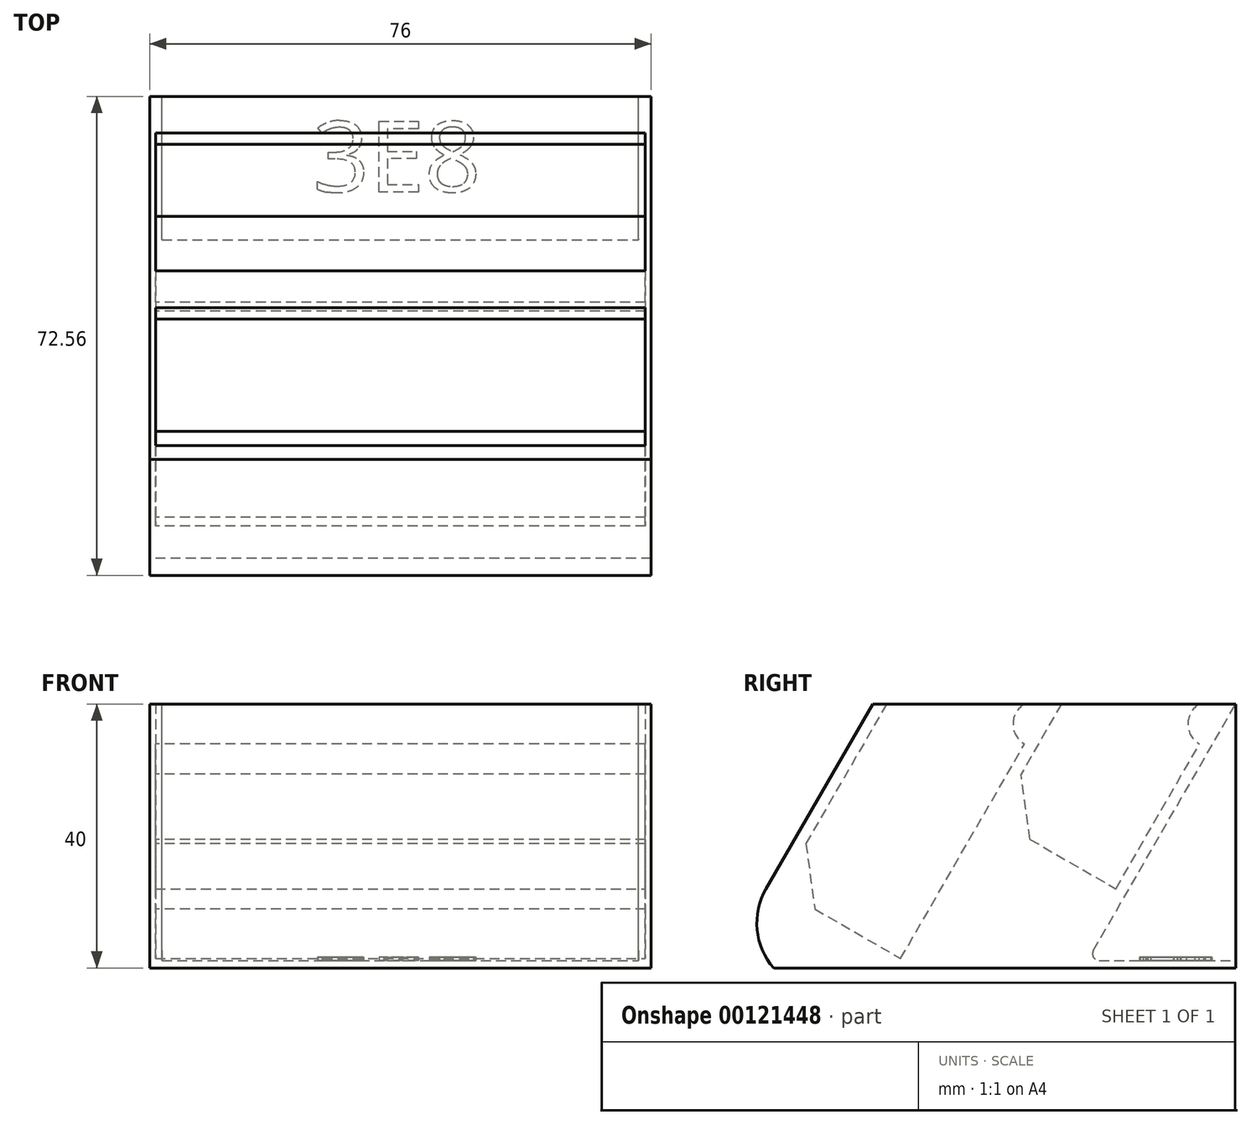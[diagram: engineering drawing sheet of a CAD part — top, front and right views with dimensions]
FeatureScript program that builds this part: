
annotation { "Feature Type Name" : "Feature", "Feature Type Description" : "" }
export const myFeature = defineFeature(function(context is Context, id is Id, definition is map)
    precondition{}
    {
        {
            var Q0;
            Q0=qCreatedBy(makeId("Right.planeOp"),FACE);
            var sketch = newSketch(context, id + "F0", { "sketchPlane" : qUnion([Q0])});
            skLineSegment(sketch, "E0", {"start": v(-35, 0) * mm, "end": v(35, 0) * mm});
            skLineSegment(sketch, "E1", {"start": v(35, 0) * mm, "end": v(35, 40) * mm});
            skLineSegment(sketch, "E2", {"start": v(35, 40) * mm, "end": v(-20, 40) * mm});
            skLineSegment(sketch, "E3", {"start": v(-20, 40) * mm, "end": v(-36.17, 11.99) * mm});
            skArc(sketch, "E4", {"start": v(-36.17, 11.99) * mm, "mid": v(-37.51, 5.8) * mm, "end": v(-35, 0) * mm});
            skSolve(sketch);
        }
        {
            var Q0;
            Q0=makeQuery(id+"F0.imprint","IMPRINT",FACE,{"disambiguationData":[TD([[makeQuery(id+"F0.imprint","IMPRINT",EDGE,{"derivedFrom":sQuery(id+"F0.wireOp",EDGE,"E0")}),1.0]])]});
            extrude(context, id + "F1", {"entities" : qUnion([Q0]), "endBound" : BoundingType.SYMMETRIC, "depth" : 76 * mm});
        }
        {
            var Q0;
            Q0=makeQuery(id+"F1.opExtrude","CAP_FACE",FACE,{"disambiguationData":[OSD([sQuery(id+"F0.wireOp",EDGE,"E0"),sQuery(id+"F0.wireOp",EDGE,"E1"),sQuery(id+"F0.wireOp",EDGE,"E2"),sQuery(id+"F0.wireOp",EDGE,"E3"),sQuery(id+"F0.wireOp",EDGE,"E4")])],"isStart":false});
            cPlane(context, id + "F2", {"entities" : qUnion([Q0]), "cplaneType" : CPlaneType.OFFSET, "offset" : .9 * mm, "oppositeDirection" : true, "width" : 150 * mm, "height" : 150 * mm});
        }
        {
            var Q0;
            Q0=qCreatedBy(id+"F2.planeOp",FACE);
            var sketch = newSketch(context, id + "F3", { "sketchPlane" : qUnion([Q0])});
            skPoint(sketch, "E5", {"position": v(-20, 40) * mm});
            skPoint(sketch, "E6", {"position": v(35, 0) * mm});
            skPoint(sketch, "E7", {"position": v(-35, 0) * mm});
            skPoint(sketch, "E8", {"position": v(-36.17, 11.99) * mm});
            skLineSegment(sketch, "E9", {"start": v(-20, 40) * mm, "end": v(-17.9, 40) * mm, "construction": true});
            skLineSegment(sketch, "E10", {"start": v(-36.17, 11.99) * mm, "end": v(-34.07, 11.99) * mm, "construction": true});
            skLineSegment(sketch, "E11", {"start": v(35.1, 40) * mm, "end": v(33, 40) * mm, "construction": true});
            skLineSegment(sketch, "E12", {"start": v(-17.9, 40) * mm, "end": v(-34.07, 11.99) * mm});
            skLineSegment(sketch, "E13", {"start": v(-34.07, 11.99) * mm, "end": v(-15.77, 1.42) * mm});
            skLineSegment(sketch, "E14", {"start": v(-15.77, 1.42) * mm, "end": v(6.5, 40) * mm});
            skLineSegment(sketch, "E15", {"start": v(6.5, 40) * mm, "end": v(8.6, 40) * mm, "construction": true});
            skLineSegment(sketch, "E16", {"start": v(12.57, 1.15) * mm, "end": v(35, 40) * mm});
            skLineSegment(sketch, "E17", {"start": v(8.6, 40) * mm, "end": v(33, 40) * mm});
            skLineSegment(sketch, "E18", {"start": v(-17.9, 40) * mm, "end": v(6.5, 40) * mm});
            skLineSegment(sketch, "E19", {"start": v(12.57, 1.15) * mm, "end": v(35, 1.15) * mm});
            skLineSegment(sketch, "E20", {"start": v(35, 1.15) * mm, "end": v(35, 40) * mm});
            skLineSegment(sketch, "E21", {"start": v(-34.07, 11.99) * mm, "end": v(16.83, 11.99) * mm, "construction": true});
            skLineSegment(sketch, "E22", {"start": v(8.6, 40) * mm, "end": v(-1.47, 22.55) * mm});
            skLineSegment(sketch, "E23", {"start": v(-1.47, 22.55) * mm, "end": v(16.83, 11.99) * mm});
            skLineSegment(sketch, "E24", {"start": v(16.83, 11.99) * mm, "end": v(33, 40) * mm});
            skSolve(sketch);
        }
        {
            var Q0;
            Q0=qSketchRegion(id+"F3",true);
            extrude(context, id + "F4", {"entities" : qUnion([Q0]), "operationType" : NewBodyOperationType.REMOVE, "oppositeDirection" : true, "depth" : 74.2 * mm});
        }
        {
            var Q0;
            Q0=makeQuery(id+"F4.boolean.opBoolean","COPY",FACE,{"derivedFrom":makeQuery(id+"F4.opExtrude","CAP_FACE",FACE,{"disambiguationData":[OSD([sQuery(id+"F3.wireOp",EDGE,"be90a4c1-fdc4-44e3-ab6c-95068b80fabc"),sQuery(id+"F3.wireOp",EDGE,"26c6214a-6b9a-4307-9401-254e5f0091ab"),sQuery(id+"F3.wireOp",EDGE,"35e6dab0-42ec-4566-bf5d-57dbf1a0a791"),sQuery(id+"F3.wireOp",EDGE,"E16")])],"isStart":true})});
            extrude(context, id + "F5", {"entities" : qUnion([Q0]), "operationType" : NewBodyOperationType.ADD, "depth" : 1 * mm});
        }
        {
            var Q0;
            Q0=makeQuery(id+"F4.boolean.opBoolean","COPY",FACE,{"derivedFrom":makeQuery(id+"F4.opExtrude","CAP_FACE",FACE,{"disambiguationData":[OSD([sQuery(id+"F3.wireOp",EDGE,"be90a4c1-fdc4-44e3-ab6c-95068b80fabc"),sQuery(id+"F3.wireOp",EDGE,"26c6214a-6b9a-4307-9401-254e5f0091ab"),sQuery(id+"F3.wireOp",EDGE,"35e6dab0-42ec-4566-bf5d-57dbf1a0a791"),sQuery(id+"F3.wireOp",EDGE,"E16")])],"isStart":false})});
            extrude(context, id + "F6", {"entities" : qUnion([Q0]), "operationType" : NewBodyOperationType.ADD, "depth" : 1 * mm});
        }
        {
            var Q0;
            Q0=makeQuery(id+"F4.boolean.opBoolean","COPY",FACE,{"derivedFrom":makeQuery(id+"F4.opExtrude","SWEPT_FACE",FACE,{"disambiguationData":[OSD([sQuery(id+"F3.wireOp",EDGE,"E19")])]})});
            var sketch = newSketch(context, id + "F7", { "sketchPlane" : qUnion([Q0])});
            skText(sketch, "E25", { "text": "3E8", "fontName": "OpenSans-Regular.ttf"});
            const initialGuessF7  = {"E25": [-0.01326, 0.02053, 1, 0, 0.01078]};
            skSetInitialGuess(sketch, initialGuessF7);
            skSolve(sketch);
        }
        {
            var Q0;
            Q0=qSketchRegion(id+"F7",true);
            extrude(context, id + "F8", {"entities" : qUnion([Q0]), "operationType" : NewBodyOperationType.ADD, "depth" : .5 * mm});
        }
        {
            var Q0;
            Q0=makeQuery(id+"F1.opExtrude","CAP_FACE",FACE,{"disambiguationData":[OSD([sQuery(id+"F0.wireOp",EDGE,"E0"),sQuery(id+"F0.wireOp",EDGE,"E1"),sQuery(id+"F0.wireOp",EDGE,"E2"),sQuery(id+"F0.wireOp",EDGE,"E3"),sQuery(id+"F0.wireOp",EDGE,"E4")])],"isStart":false});
            var sketch = newSketch(context, id + "F9", { "sketchPlane" : qUnion([Q0])});
            skPoint(sketch, "E26.0", {"position": v(35.1, 40) * mm});
            skLineSegment(sketch, "E27", {"start": v(35.1, 40) * mm, "end": v(16.83, 8.35) * mm});
            skLineSegment(sketch, "E28", {"start": v(15.18, 9.3) * mm, "end": v(16.83, 8.35) * mm});
            skLineSegment(sketch, "E29", {"start": v(15.18, 9.3) * mm, "end": v(32.9, 40) * mm});
            skLineSegment(sketch, "E30", {"start": v(35.1, 40) * mm, "end": v(32.9, 40) * mm});
            skLineSegment(sketch, "E31", {"start": v(35, 40) * mm, "end": v(32.9, 40) * mm, "construction": true});
            skLineSegment(sketch, "E32.0", {"start": v(16.83, 11.99) * mm, "end": v(33, 40) * mm, "construction": true});
            skLineSegment(sketch, "E33", {"start": v(16.83, 11.99) * mm, "end": v(16.83, 8.35) * mm, "construction": true});
            skLineSegment(sketch, "E34.0", {"start": v(-1.47, 22.55) * mm, "end": v(16.83, 11.99) * mm, "construction": true});
            skLineSegment(sketch, "E35", {"start": v(7.68, 17.27) * mm, "end": v(3.68, 10.34) * mm, "construction": true});
            skCircle(sketch, "E36", {"center": v(3.68, 10.34) * mm, "radius": 2.5 * mm, "construction": true});
            skLineSegment(sketch, "E37.0", {"start": v(-34.07, 11.99) * mm, "end": v(-15.77, 1.42) * mm, "construction": true});
            skLineSegment(sketch, "E38", {"start": v(-24.92, 6.7) * mm, "end": v(-26.92, 3.24) * mm, "construction": true});
            skCircle(sketch, "E39", {"center": v(-26.92, 3.24) * mm, "radius": 2.5 * mm, "construction": true});
            skSolve(sketch);
        }
        {
            var Q0;
            Q0=makeQuery(id+"FucgoeEpTm8NwyI_1.boolean.opBoolean","COPY",EDGE,{"derivedFrom":makeQuery(id+"FucgoeEpTm8NwyI_1.opExtrude","SWEPT_EDGE",EDGE,{"disambiguationData":[OSD([sQuery(id+"F0.wireOp",EDGE,"E2"),sQuery(id+"F9.wireOp",EDGE,"E29"),sQuery(id+"F9.wireOp",EDGE,"E30")])]})});
            var Q1;
            Q1=makeQuery(id+"FucgoeEpTm8NwyI_1.boolean.opBoolean","COPY",EDGE,{"derivedFrom":makeQuery(id+"FucgoeEpTm8NwyI_1.opExtrude","SWEPT_EDGE",EDGE,{"disambiguationData":[OSD([sQuery(id+"F0.wireOp",EDGE,"E2"),sQuery(id+"F9.wireOp",EDGE,"E27"),sQuery(id+"F9.wireOp",EDGE,"E30")])]})});
            var Q2;
            Q2=makeQuery(id+"FucgoeEpTm8NwyI_1.boolean.opBoolean","COPY",EDGE,{"derivedFrom":makeQuery(id+"FucgoeEpTm8NwyI_1.opExtrude","SWEPT_EDGE",EDGE,{"disambiguationData":[OSD([sQuery(id+"F9.wireOp",EDGE,"E27"),sQuery(id+"F9.wireOp",EDGE,"E28")])]})});
            var Q3;
            Q3=makeQuery(id+"FucgoeEpTm8NwyI_1.boolean.opBoolean","COPY",EDGE,{"derivedFrom":makeQuery(id+"FucgoeEpTm8NwyI_1.opExtrude","SWEPT_EDGE",EDGE,{"disambiguationData":[OSD([sQuery(id+"F9.wireOp",EDGE,"E28"),sQuery(id+"F9.wireOp",EDGE,"E29")])]})});
            var Q4;
            Q4=makeQuery(id+"F4.boolean.opBoolean","COPY",EDGE,{"derivedFrom":makeQuery(id+"F4.opExtrude","SWEPT_EDGE",EDGE,{"disambiguationData":[OSD([sQuery(id+"F3.wireOp",EDGE,"E16"),sQuery(id+"F3.wireOp",EDGE,"E19")])]})});
            fillet(context, id + "F10", {"entities" : qUnion([Q0, Q1, Q2, Q3, Q4]), "radius" : 1 * mm, "tangentPropagation" : true, "allowEdgeOverflow" : false});
        }
        {
            var Q0;
            Q0=makeQuery(id+"F4.boolean.opBoolean","COPY",FACE,{"derivedFrom":makeQuery(id+"F4.opExtrude","CAP_FACE",FACE,{"disambiguationData":[OSD([sQuery(id+"F3.wireOp",EDGE,"E17"),sQuery(id+"F3.wireOp",EDGE,"E22"),sQuery(id+"F3.wireOp",EDGE,"E23"),sQuery(id+"F3.wireOp",EDGE,"E24")])],"isStart":false})});
            var sketch = newSketch(context, id + "F11", { "sketchPlane" : qUnion([Q0])});
            skLineSegment(sketch, "E40", {"start": v(33, 40) * mm, "end": v(29.5, 33.94) * mm});
            skArc(sketch, "E41", {"start": v(33, 40) * mm, "mid": v(28.22, 38.72) * mm, "end": v(29.5, 33.94) * mm});
            skPoint(sketch, "E42.0", {"position": v(6.5, 40) * mm});
            skLineSegment(sketch, "E43.0", {"start": v(-15.77, 1.42) * mm, "end": v(6.5, 40) * mm, "construction": true});
            skLineSegment(sketch, "E44", {"start": v(6.5, 40) * mm, "end": v(3, 33.94) * mm});
            skArc(sketch, "E45", {"start": v(6.5, 40) * mm, "mid": v(1.72, 38.72) * mm, "end": v(3, 33.94) * mm});
            skLineSegment(sketch, "E46.0", {"start": v(-17.9, 40) * mm, "end": v(6.5, 40) * mm});
            skLineSegment(sketch, "E47.0", {"start": v(8.6, 40) * mm, "end": v(33, 40) * mm});
            skLineSegment(sketch, "E48", {"start": v(16.83, 11.99) * mm, "end": v(3.84, 19.49) * mm, "construction": true});
            skLineSegment(sketch, "E49", {"start": v(3.84, 19.49) * mm, "end": v(2.48, 29.4) * mm});
            skLineSegment(sketch, "E50", {"start": v(2.48, 29.4) * mm, "end": v(-1.47, 22.55) * mm});
            skLineSegment(sketch, "E51", {"start": v(-1.47, 22.55) * mm, "end": v(3.84, 19.49) * mm});
            skPoint(sketch, "E52.0", {"position": v(-34.07, 11.99) * mm});
            skLineSegment(sketch, "E53", {"start": v(-15.77, 1.42) * mm, "end": v(-28.76, 8.92) * mm, "construction": true});
            skLineSegment(sketch, "E54", {"start": v(-28.76, 8.92) * mm, "end": v(-34.07, 11.99) * mm});
            skLineSegment(sketch, "E55", {"start": v(-34.07, 11.99) * mm, "end": v(-30.12, 18.83) * mm});
            skLineSegment(sketch, "E56", {"start": v(-30.12, 18.83) * mm, "end": v(-28.76, 8.92) * mm});
            skSolve(sketch);
        }
        {
            var Q0;
            {var subQ0=sQuery(id+"F11.wireOp",EDGE,"E44");Q0=makeQuery(id+"F11.imprint","IMPRINT",FACE,{"disambiguationData":[TD([[makeQuery(id+"F11.imprint","IMPRINT",EDGE,{"derivedFrom":subQ0}),-1.0]])]});}
            var Q1;
            {var subQ0=sQuery(id+"F11.wireOp",EDGE,"E40");Q1=makeQuery(id+"F11.imprint","IMPRINT",FACE,{"disambiguationData":[TD([[makeQuery(id+"F11.imprint","IMPRINT",EDGE,{"derivedFrom":subQ0}),1.0]])]});}
            var Q2;
            Q2=makeQuery(id+"F11.imprint","IMPRINT",FACE,{"disambiguationData":[TD([[makeQuery(id+"F11.imprint","IMPRINT",EDGE,{"derivedFrom":sQuery(id+"F11.wireOp",EDGE,"E49")}),1.0]])]});
            var Q3;
            Q3=makeQuery(id+"F11.imprint","IMPRINT",FACE,{"disambiguationData":[TD([[makeQuery(id+"F11.imprint","IMPRINT",EDGE,{"derivedFrom":sQuery(id+"F11.wireOp",EDGE,"E54")}),-1.0]])]});
            extrude(context, id + "F12", {"entities" : qUnion([Q0, Q1, Q2, Q3]), "operationType" : NewBodyOperationType.ADD, "endBound" : BoundingType.UP_TO_NEXT, "depth" : 25 * mm});
        }
    });
